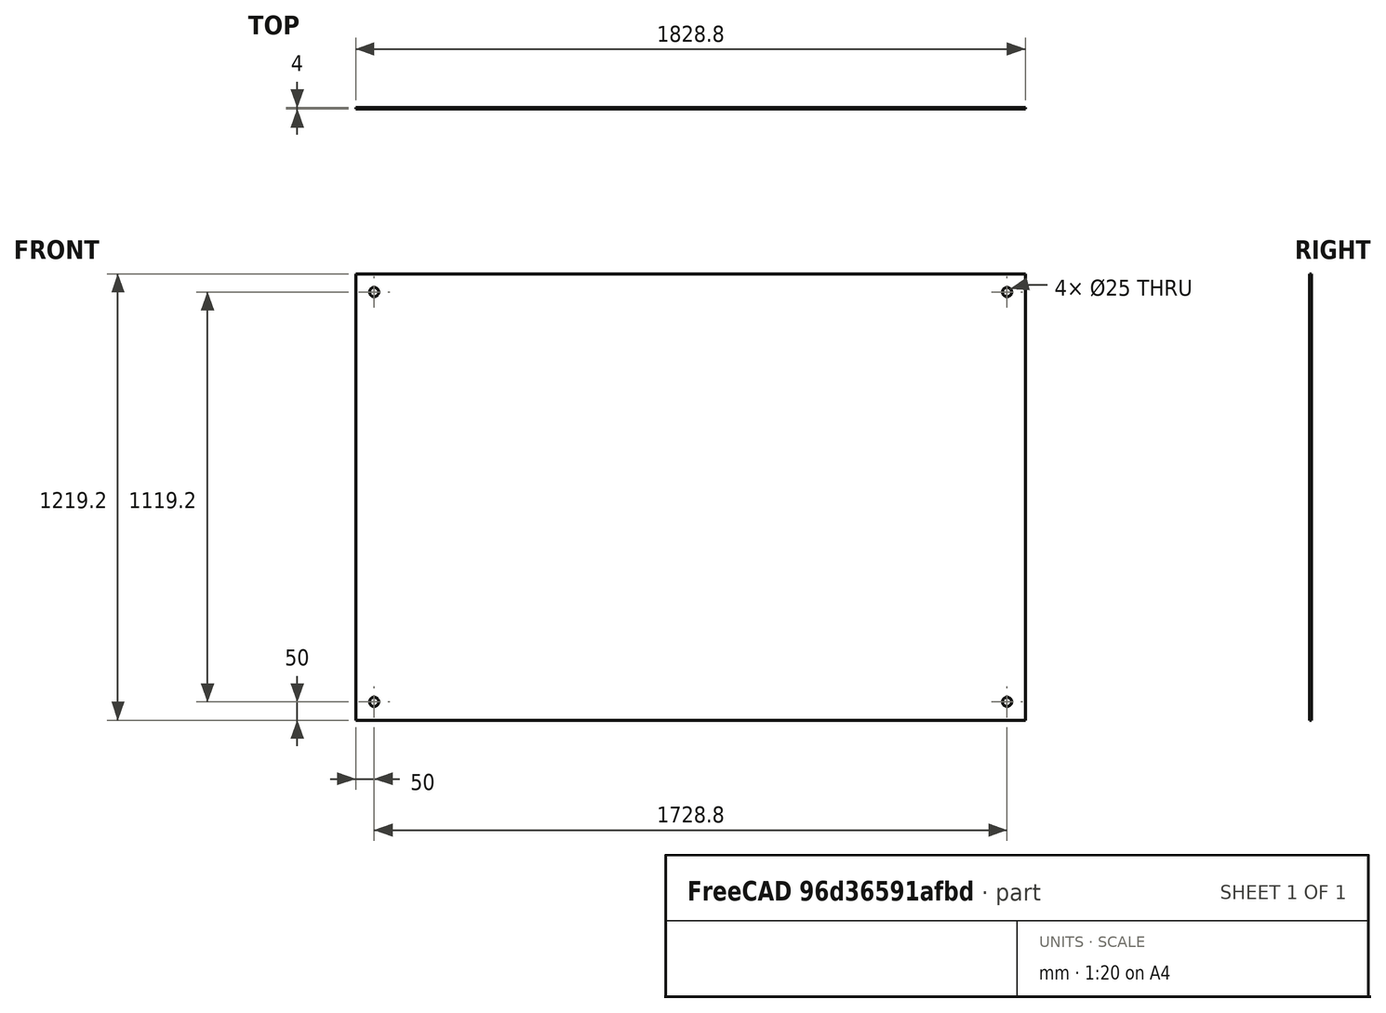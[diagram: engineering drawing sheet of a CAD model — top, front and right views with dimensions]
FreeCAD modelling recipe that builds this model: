
FCSTD DOCUMENT  (FreeCAD 0.19R24291 (Git))
Label: whiteBoard-6x4
License: All rights reserved
LicenseURL: http://en.wikipedia.org/wiki/All_rights_reserved
objects: Sketcher::SketchObject×1, PartDesign::Pad×1, PartDesign::Body×1
note: 4 computed .brp shape members not serialized (recipe doc carries the construction recipe); baked Part::Feature solids carry a one-line shape summary decoded from their .brp

FEATURE [Sketcher::SketchObject] Sketch
  FullyConstrained = false
  MapMode = 5
  Placement = pos=(0,0,0) rot=(1,0,0;1.5708rad)
  Support = -> [XZ_Plane]
  expr: Constraints[9] = 6 * 12 * 25.4
  expr: Constraints[10] = 48 * 25.4
  sketch-geometry (10):
    g0: LineSegment StartX=0 StartY=0 StartZ=0 EndX=1828.8 EndY=0 EndZ=0
    g1: LineSegment StartX=1828.8 StartY=0 StartZ=0 EndX=1828.8 EndY=1219.2 EndZ=0
    g2: LineSegment StartX=1828.8 StartY=1219.2 StartZ=0 EndX=0 EndY=1219.2 EndZ=0
    g3: LineSegment StartX=0 StartY=1219.2 StartZ=0 EndX=0 EndY=0 EndZ=0
    g4: Circle CenterX=50 CenterY=50 CenterZ=0 NormalX=0 NormalY=0 NormalZ=1 AngleXU=0 Radius=12.5
    g5: LineSegment StartX=914.4 StartY=0 StartZ=0 EndX=914.4 EndY=1219.2 EndZ=0
    g6: LineSegment StartX=-3e-16 StartY=609.6 StartZ=0 EndX=1828.8 EndY=609.6 EndZ=0
    g7: Circle CenterX=1778.8 CenterY=50 CenterZ=0 NormalX=0 NormalY=0 NormalZ=1 AngleXU=0 Radius=12.5
    g8: Circle CenterX=50 CenterY=1169.2 CenterZ=0 NormalX=0 NormalY=0 NormalZ=1 AngleXU=0 Radius=12.5
    g9: Circle CenterX=1778.8 CenterY=1169.2 CenterZ=0 NormalX=0 NormalY=0 NormalZ=1 AngleXU=0 Radius=12.5
  constraints (23):
    c: Coincident(g0,g1)
    c: Coincident(g1,g2)
    c: Coincident(g2,g3)
    c: Coincident(g3,g0)
    c: Horizontal(g0)
    c: Horizontal(g2)
    c: Vertical(g1)
    c: Vertical(g3)
    c: Coincident(g0,g-1)
    c: DistanceX(g0,g0) = 1828.8
    c: DistanceY(g3,g3) = 1219.2
    c: DistanceY(g0,g4) = 50
    c: DistanceX(g0,g4) = 50
    c: Diameter(g4) = 25
    c: Vertical(g5)
    c: Symmetric(g0,g0,g5)
    c: PointOnObject(g5,g2)
    c: Horizontal(g6)
    c: Symmetric(g2,g0,g6)
    c: PointOnObject(g6,g1)
    c: Diameter(g7) = 25
    c: Diameter(g8) = 25
    c: Diameter(g9) = 25
FEATURE [PartDesign::Pad] Pad
  Direction = (1,1,1)
  Length = 4
  Length2 = 100
  Placement = pos=(0,0,0) rot=(1,0,0;1.5708rad)
  Profile = -> Sketch
  Type = 0
FEATURE [PartDesign::Body] Body
  Group = -> [Sketch,Pad]
  Origin = -> Origin
  Tip = -> Pad
